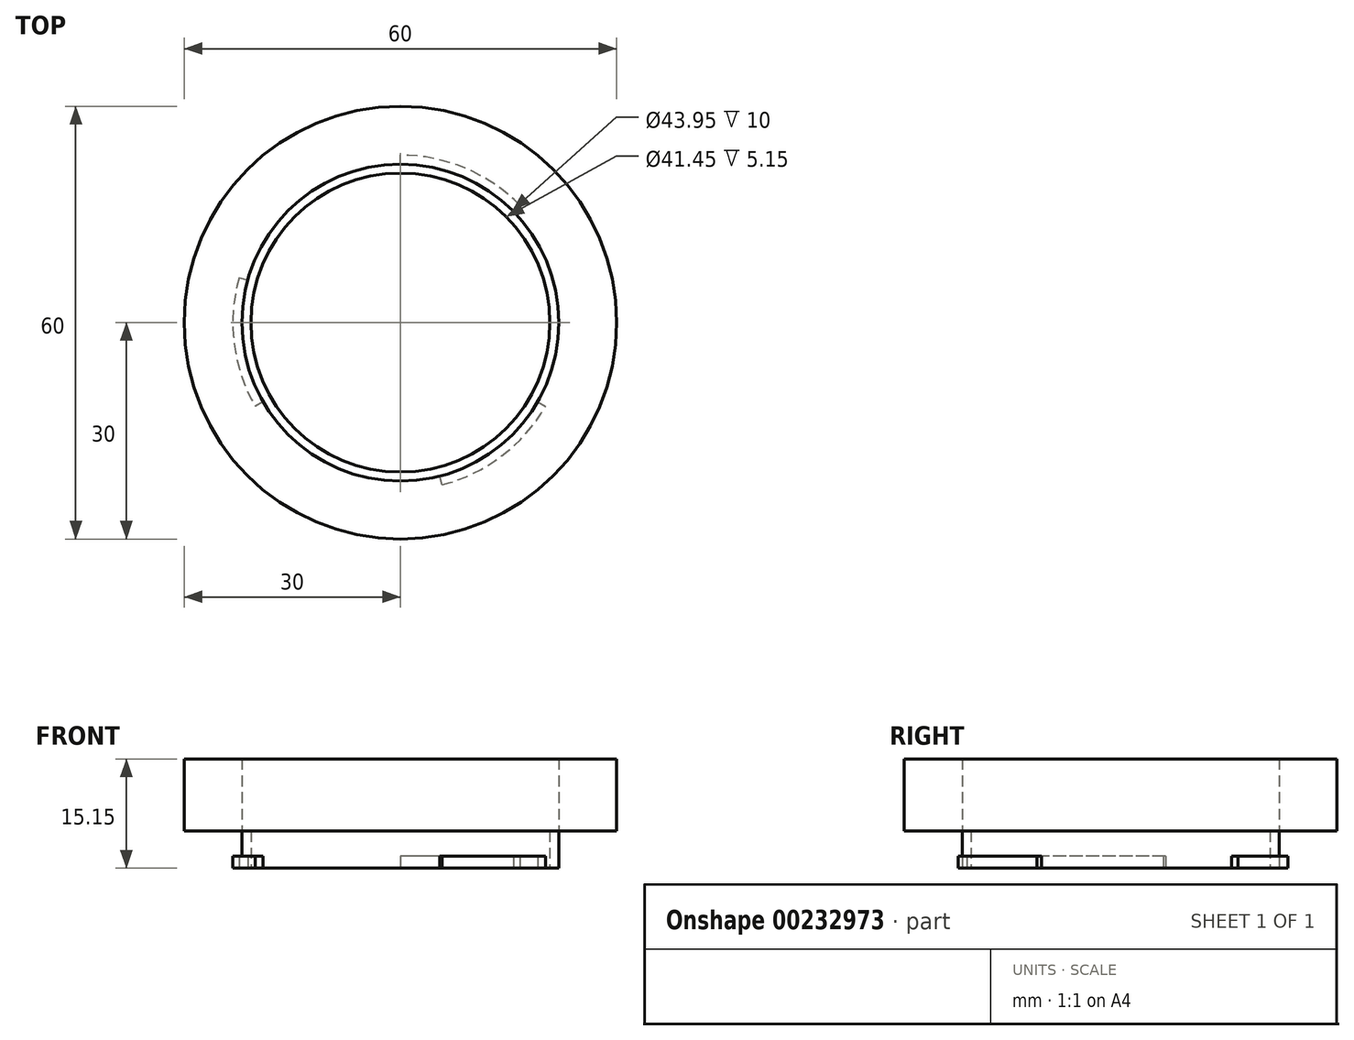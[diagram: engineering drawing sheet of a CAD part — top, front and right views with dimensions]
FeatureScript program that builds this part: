
annotation { "Feature Type Name" : "Feature", "Feature Type Description" : "" }
export const myFeature = defineFeature(function(context is Context, id is Id, definition is map)
    precondition{}
    {
        {
            assignVariable(context, id + "F0", {"name" : "Nasen_dicke", "anyValue" : 1.7});
        }
        {
            assignVariable(context, id + "F1", {"name" : "Ring_hoehe", "anyValue" : 5.15});
        }
        {
            assignVariable(context, id + "F2", {"name" : "Aufsatz_hoehe", "anyValue" : 10});
        }
        {
            var Q0;
            Q0=qCreatedBy(makeId("Top.planeOp"),FACE);
            var sketch = newSketch(context, id + "F3", { "sketchPlane" : qUnion([Q0])});
            skCircle(sketch, "E0", {"center": v(0, 0) * mm, "radius": 20.73 * mm});
            skCircle(sketch, "E1", {"center": v(0, 0) * mm, "radius": 21.98 * mm});
            skLineSegment(sketch, "E2", {"start": v(0, 20.73) * mm, "end": v(0, 21.98) * mm});
            skLineSegment(sketch, "E3", {"start": v(0, 21.98) * mm, "end": v(0, 23.23) * mm});
            skArc(sketch, "E4", {"start": v(16.6, 16.25) * mm, "mid": v(9, 21.41) * mm, "end": v(0, 23.23) * mm});
            skLineSegment(sketch, "E5", {"start": v(16.6, 16.25) * mm, "end": v(15.7, 15.38) * mm});
            skLineSegment(sketch, "E6.1.0", {"start": v(-22.37, 6.25) * mm, "end": v(-21.17, 5.9) * mm});
            skArc(sketch, "E6.1.1", {"start": v(-22.37, 6.25) * mm, "mid": v(-23.04, -2.91) * mm, "end": v(-20.11, -11.61) * mm});
            skLineSegment(sketch, "E6.1.2", {"start": v(-19.03, -10.99) * mm, "end": v(-20.11, -11.61) * mm});
            skLineSegment(sketch, "E6.2.0", {"start": v(5.78, -22.5) * mm, "end": v(5.47, -21.28) * mm});
            skArc(sketch, "E6.2.1", {"start": v(5.78, -22.5) * mm, "mid": v(14.04, -18.5) * mm, "end": v(20.11, -11.61) * mm});
            skLineSegment(sketch, "E6.2.2", {"start": v(19.03, -10.99) * mm, "end": v(20.11, -11.61) * mm});
            skSolve(sketch);
        }
        {
            var Q0;
            Q0=makeQuery(id+"F3.imprint","IMPRINT",FACE,{"disambiguationData":[TD([[makeQuery(id+"F3.imprint","IMPRINT",EDGE,{"derivedFrom":sQuery(id+"F3.wireOp",EDGE,"E0")}),-1.0]])]});
            extrude(context, id + "F4", {"entities" : qUnion([Q0]), "depth" : (getVariable(context, 'Ring_hoehe')) * mm});
        }
        {
            var Q0;
            {var subQ0=sQuery(id+"F3.wireOp",EDGE,"E6.1.0");Q0=makeQuery(id+"F3.imprint","IMPRINT",FACE,{"disambiguationData":[TD([[makeQuery(id+"F3.imprint","IMPRINT",EDGE,{"derivedFrom":subQ0}),-1.0]])]});}
            var Q1;
            {var subQ0=sQuery(id+"F3.wireOp",EDGE,"E3");Q1=makeQuery(id+"F3.imprint","IMPRINT",FACE,{"disambiguationData":[TD([[makeQuery(id+"F3.imprint","IMPRINT",EDGE,{"derivedFrom":subQ0}),-1.0]])]});}
            var Q2;
            {var subQ0=sQuery(id+"F3.wireOp",EDGE,"E6.2.0");Q2=makeQuery(id+"F3.imprint","IMPRINT",FACE,{"disambiguationData":[TD([[makeQuery(id+"F3.imprint","IMPRINT",EDGE,{"derivedFrom":subQ0}),-1.0]])]});}
            extrude(context, id + "F5", {"entities" : qUnion([Q0, Q1, Q2]), "operationType" : NewBodyOperationType.ADD, "depth" : (getVariable(context, 'Nasen_dicke')) * mm});
        }
        {
            var Q0;
            Q0=makeQuery(id+"F4.opExtrude","CAP_FACE",FACE,{"disambiguationData":[OSD([sQuery(id+"F3.wireOp",EDGE,"E0"),sQuery(id+"F3.wireOp",EDGE,"E1")])],"isStart":false});
            var sketch = newSketch(context, id + "F6", { "sketchPlane" : qUnion([Q0])});
            skCircle(sketch, "E7", {"center": v(0, 0) * mm, "radius": 30 * mm});
            skSolve(sketch);
        }
        {
            var Q0;
            Q0=makeQuery(id+"F6.imprint","IMPRINT",FACE,{"disambiguationData":[TD([[makeQuery(id+"F6.imprint","IMPRINT",EDGE,{"derivedFrom":sQuery(id+"F6.wireOp",EDGE,"E7")}),1.0]])]});
            extrude(context, id + "F7", {"entities" : qUnion([Q0]), "depth" : (getVariable(context, 'Aufsatz_hoehe')) * mm});
        }
    });
